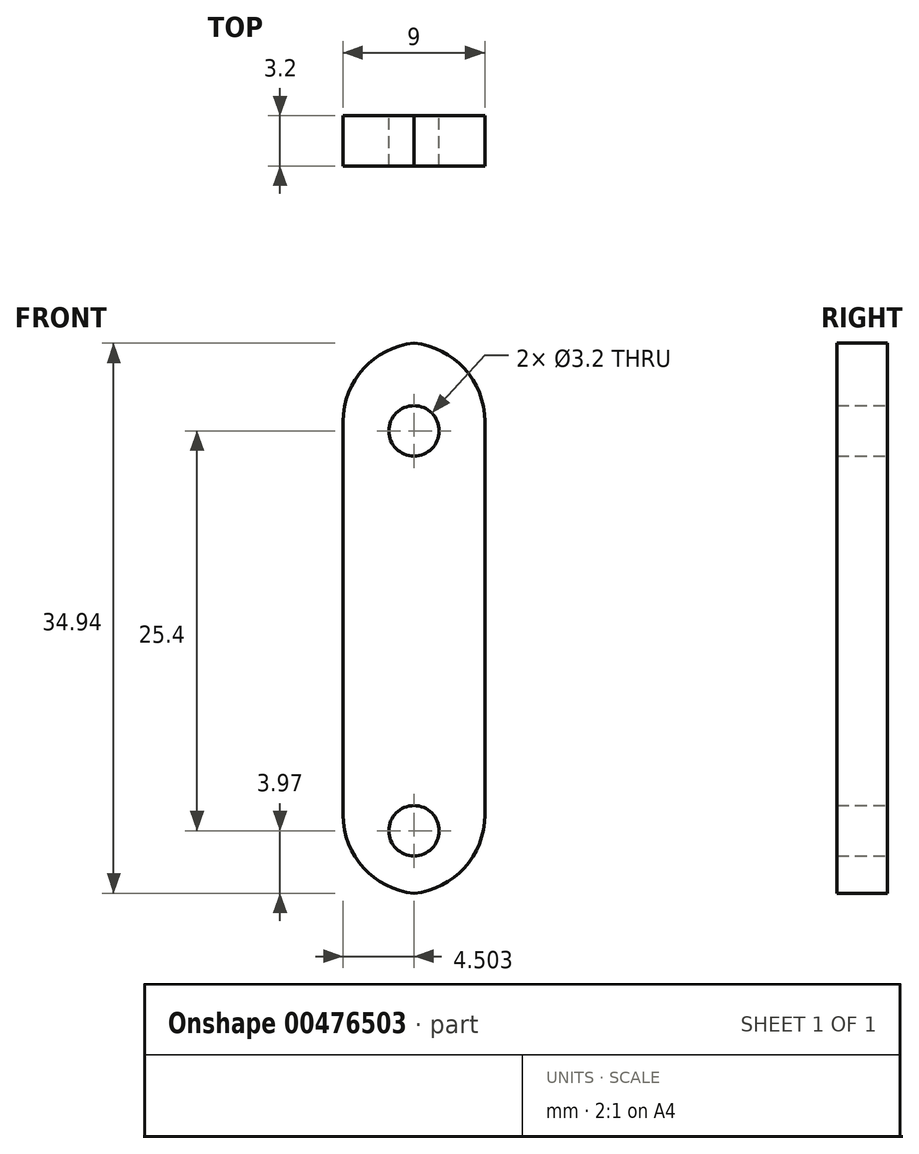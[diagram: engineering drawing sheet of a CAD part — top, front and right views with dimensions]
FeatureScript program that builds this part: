
annotation { "Feature Type Name" : "Feature", "Feature Type Description" : "" }
export const myFeature = defineFeature(function(context is Context, id is Id, definition is map)
    precondition{}
    {
        {
            var Q0;
            Q0=qCreatedBy(makeId("Front.planeOp"),FACE);
            var sketch = newSketch(context, id + "F0", { "sketchPlane" : qUnion([Q0])});
            skLineSegment(sketch, "E0.bottom", {"start": v(-19.24, 31) * mm, "end": v(-10.24, 31) * mm});
            skLineSegment(sketch, "E0.top", {"start": v(-19.24, -4) * mm, "end": v(-10.24, -4) * mm});
            skLineSegment(sketch, "E0.left", {"start": v(-19.24, 31) * mm, "end": v(-19.24, -4) * mm});
            skLineSegment(sketch, "E0.right", {"start": v(-10.24, 31) * mm, "end": v(-10.24, -4) * mm});
            skCircle(sketch, "E1", {"center": v(-14.74, 0) * mm, "radius": 1.6 * mm});
            skPoint(sketch, "E1.centerSnap0", {"position": v(-14.74, -4) * mm});
            skCircle(sketch, "E2", {"center": v(-14.74, 25.4) * mm, "radius": 1.6 * mm});
            skSolve(sketch);
        }
        {
            var Q0;
            Q0 = qSketchRegion(id + "F0", true);
            extrude(context, id + "F1", {"entities" : qUnion([Q0]), "depth" : 3.2 * mm, "offsetDistance" : 25 * mm});
        }
        {
            var Q0;
            Q0=makeQuery(id+"F1.opExtrude","SWEPT_EDGE",EDGE,{"disambiguationData":[OSD([sQuery(id+"F0.wireOp",EDGE,"E0.bottom"),sQuery(id+"F0.wireOp",EDGE,"E0.right")])]});
            var Q1;
            Q1=makeQuery(id+"F1.opExtrude","SWEPT_EDGE",EDGE,{"disambiguationData":[OSD([sQuery(id+"F0.wireOp",EDGE,"E0.bottom"),sQuery(id+"F0.wireOp",EDGE,"E0.left")])]});
            var Q2;
            Q2=makeQuery(id+"F1.opExtrude","SWEPT_EDGE",EDGE,{"disambiguationData":[OSD([sQuery(id+"F0.wireOp",EDGE,"E0.top"),sQuery(id+"F0.wireOp",EDGE,"E0.right")])]});
            var Q3;
            Q3=makeQuery(id+"F1.opExtrude","SWEPT_EDGE",EDGE,{"disambiguationData":[OSD([sQuery(id+"F0.wireOp",EDGE,"E0.top"),sQuery(id+"F0.wireOp",EDGE,"E0.left")])]});
            fillet(context, id + "F2", {"entities" : qUnion([Q0, Q1, Q2, Q3]), "radius" : 5 * mm, "tangentPropagation" : true, "allowEdgeOverflow" : false});
        }
    });
